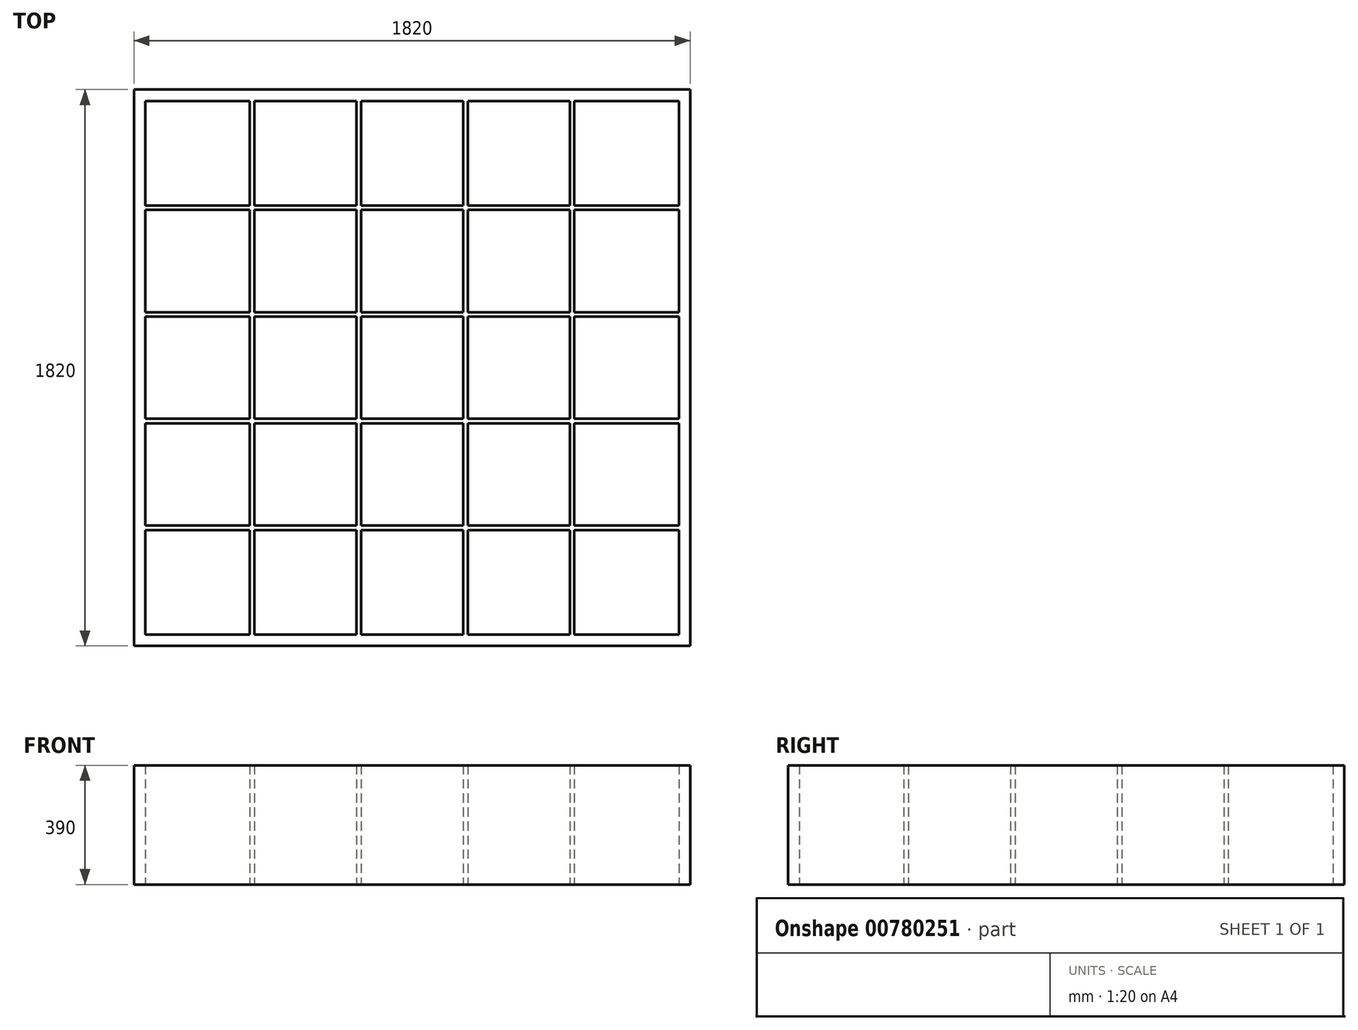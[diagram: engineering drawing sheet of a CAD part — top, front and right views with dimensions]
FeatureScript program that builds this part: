
annotation { "Feature Type Name" : "Feature", "Feature Type Description" : "" }
export const myFeature = defineFeature(function(context is Context, id is Id, definition is map)
    precondition{}
    {
        {
            var Q0;
            Q0=qCreatedBy(makeId("Top.planeOp"),FACE);
            var sketch = newSketch(context, id + "F0", { "sketchPlane" : qUnion([Q0])});
            skLineSegment(sketch, "E0.bottom", {"start": v(910, 910) * mm, "end": v(-910, 910) * mm});
            skLineSegment(sketch, "E0.top", {"start": v(910, -910) * mm, "end": v(-910, -910) * mm});
            skLineSegment(sketch, "E0.left", {"start": v(910, 910) * mm, "end": v(910, -910) * mm});
            skLineSegment(sketch, "E0.right", {"start": v(-910, 910) * mm, "end": v(-910, -910) * mm});
            skPoint(sketch, "E0.middle", {"position": v(0, 0) * mm});
            skLineSegment(sketch, "E1.0", {"start": v(-873, 873) * mm, "end": v(-873, 531.3) * mm});
            skLineSegment(sketch, "E1.1", {"start": v(873, 873) * mm, "end": v(531.3, 873) * mm});
            skLineSegment(sketch, "E1.2", {"start": v(873, 873) * mm, "end": v(873, 531.3) * mm});
            skLineSegment(sketch, "E1.3", {"start": v(873, -873) * mm, "end": v(531.3, -873) * mm});
            skLineSegment(sketch, "E2", {"start": v(-523.8, -873) * mm, "end": v(-523.8, 873) * mm, "construction": true});
            skLineSegment(sketch, "E3.0", {"start": v(-516.3, -873) * mm, "end": v(-516.3, 873) * mm});
            skLineSegment(sketch, "E4.0", {"start": v(-531.3, -873) * mm, "end": v(-531.3, 873) * mm});
            skLineSegment(sketch, "E5.1.0.0", {"start": v(-167.1, -873) * mm, "end": v(-167.1, 873) * mm});
            skLineSegment(sketch, "E5.1.0.1", {"start": v(-174.6, -873) * mm, "end": v(-174.6, 873) * mm, "construction": true});
            skLineSegment(sketch, "E5.1.0.2", {"start": v(-182.1, -873) * mm, "end": v(-182.1, 873) * mm});
            skLineSegment(sketch, "E5.2.0.0", {"start": v(182.1, -873) * mm, "end": v(182.1, 873) * mm});
            skLineSegment(sketch, "E5.2.0.1", {"start": v(174.6, -873) * mm, "end": v(174.6, 873) * mm, "construction": true});
            skLineSegment(sketch, "E5.2.0.2", {"start": v(167.1, -873) * mm, "end": v(167.1, 873) * mm});
            skLineSegment(sketch, "E5.3.0.0", {"start": v(531.3, -873) * mm, "end": v(531.3, 873) * mm});
            skLineSegment(sketch, "E5.3.0.1", {"start": v(523.8, -873) * mm, "end": v(523.8, 873) * mm, "construction": true});
            skLineSegment(sketch, "E5.3.0.2", {"start": v(516.3, -873) * mm, "end": v(516.3, 873) * mm});
            skLineSegment(sketch, "E5.direction1", {"start": v(-516.3, -873) * mm, "end": v(-182.1, -873) * mm, "construction": true});
            skLineSegment(sketch, "E6", {"start": v(-873, -523.8) * mm, "end": v(873, -523.8) * mm, "construction": true});
            skLineSegment(sketch, "E7.0", {"start": v(-873, -531.3) * mm, "end": v(873, -531.3) * mm});
            skLineSegment(sketch, "E8.0", {"start": v(-873, -516.3) * mm, "end": v(873, -516.3) * mm});
            skLineSegment(sketch, "E9.0.1.0", {"start": v(-873, -167.1) * mm, "end": v(873, -167.1) * mm});
            skLineSegment(sketch, "E9.0.1.1", {"start": v(-873, -182.1) * mm, "end": v(873, -182.1) * mm});
            skLineSegment(sketch, "E9.0.1.2", {"start": v(-873, -174.6) * mm, "end": v(873, -174.6) * mm, "construction": true});
            skLineSegment(sketch, "E9.0.2.0", {"start": v(-873, 182.1) * mm, "end": v(873, 182.1) * mm});
            skLineSegment(sketch, "E9.0.2.1", {"start": v(-873, 167.1) * mm, "end": v(873, 167.1) * mm});
            skLineSegment(sketch, "E9.0.2.2", {"start": v(-873, 174.6) * mm, "end": v(873, 174.6) * mm, "construction": true});
            skLineSegment(sketch, "E9.0.3.0", {"start": v(-873, 531.3) * mm, "end": v(873, 531.3) * mm});
            skLineSegment(sketch, "E9.0.3.1", {"start": v(-873, 516.3) * mm, "end": v(873, 516.3) * mm});
            skLineSegment(sketch, "E9.0.3.2", {"start": v(-873, 523.8) * mm, "end": v(873, 523.8) * mm, "construction": true});
            skLineSegment(sketch, "E9.direction1", {"start": v(-873, -531.3) * mm, "end": v(-848, -531.3) * mm, "construction": true});
            skLineSegment(sketch, "E10.trimOffspring", {"start": v(873, 516.3) * mm, "end": v(873, 182.1) * mm});
            skLineSegment(sketch, "E11.trimOffspring", {"start": v(873, 167.1) * mm, "end": v(873, -167.1) * mm});
            skLineSegment(sketch, "E12.trimOffspring", {"start": v(-531.3, -873) * mm, "end": v(-873, -873) * mm});
            skLineSegment(sketch, "E13.trimOffspring", {"start": v(-182.1, -873) * mm, "end": v(-516.3, -873) * mm});
            skLineSegment(sketch, "E14.trimOffspring", {"start": v(167.1, -873) * mm, "end": v(-167.1, -873) * mm});
            skLineSegment(sketch, "E15.trimOffspring", {"start": v(-873, -516.3) * mm, "end": v(-873, -182.1) * mm, "construction": true});
            skLineSegment(sketch, "E16.trimOffspring", {"start": v(-873, -531.3) * mm, "end": v(-873, -873) * mm});
            skLineSegment(sketch, "E17.trimOffspring", {"start": v(-873, -182.1) * mm, "end": v(-873, -516.3) * mm});
            skLineSegment(sketch, "E18.trimOffspring", {"start": v(-873, 167.1) * mm, "end": v(-873, -167.1) * mm});
            skLineSegment(sketch, "E19.trimOffspring", {"start": v(-873, 516.3) * mm, "end": v(-873, 182.1) * mm});
            skLineSegment(sketch, "E20.trimOffspring", {"start": v(-531.3, 873) * mm, "end": v(-873, 873) * mm});
            skLineSegment(sketch, "E21.trimOffspring", {"start": v(-182.1, 873) * mm, "end": v(-516.3, 873) * mm});
            skLineSegment(sketch, "E22.trimOffspring", {"start": v(167.1, 873) * mm, "end": v(-167.1, 873) * mm});
            skLineSegment(sketch, "E23.trimOffspring", {"start": v(516.3, 873) * mm, "end": v(182.1, 873) * mm});
            skLineSegment(sketch, "E24.trimOffspring", {"start": v(873, -182.1) * mm, "end": v(873, -516.3) * mm});
            skLineSegment(sketch, "E25.trimOffspring", {"start": v(873, -531.3) * mm, "end": v(873, -873) * mm});
            skLineSegment(sketch, "E26.trimOffspring", {"start": v(516.3, -873) * mm, "end": v(182.1, -873) * mm});
            skSolve(sketch);
        }
        {
            var Q0;
            Q0 = qSketchRegion(id + "F0", true);
            var Q1;
            {var subQ0=sQuery(id+"F0.wireOp",EDGE,"E7.0");var subQ1=sQuery(id+"F0.wireOp",EDGE,"E3.0");var subQ2=makeQuery(id+"F0.imprint","INTERSECT",VERTEX,{"derivedFrom":[subQ1,subQ0]});Q1=makeQuery(id+"F0.imprint","IMPRINT",FACE,{"disambiguationData":[TD([[makeQuery(id+"F0.imprint","IMPRINT",EDGE,{"disambiguationData":[TD([[subQ2,-1.0]])],"derivedFrom":subQ1}),-1.0]])]});}
            var Q2;
            {var subQ0=sQuery(id+"F0.wireOp",EDGE,"E7.0");var subQ1=sQuery(id+"F0.wireOp",EDGE,"E5.1.0.0");var subQ2=makeQuery(id+"F0.imprint","INTERSECT",VERTEX,{"derivedFrom":[subQ1,subQ0]});Q2=makeQuery(id+"F0.imprint","IMPRINT",FACE,{"disambiguationData":[TD([[makeQuery(id+"F0.imprint","IMPRINT",EDGE,{"disambiguationData":[TD([[subQ2,-1.0]])],"derivedFrom":subQ1}),1.0]])]});}
            var Q3;
            {var subQ0=sQuery(id+"F0.wireOp",EDGE,"E7.0");var subQ1=sQuery(id+"F0.wireOp",EDGE,"E5.1.0.0");var subQ2=makeQuery(id+"F0.imprint","INTERSECT",VERTEX,{"derivedFrom":[subQ1,subQ0]});Q3=makeQuery(id+"F0.imprint","IMPRINT",FACE,{"disambiguationData":[TD([[makeQuery(id+"F0.imprint","IMPRINT",EDGE,{"disambiguationData":[TD([[subQ2,-1.0]])],"derivedFrom":subQ1}),-1.0]])]});}
            var Q4;
            {var subQ0=sQuery(id+"F0.wireOp",EDGE,"E8.0");var subQ1=sQuery(id+"F0.wireOp",EDGE,"E5.1.0.0");var subQ2=makeQuery(id+"F0.imprint","INTERSECT",VERTEX,{"derivedFrom":[subQ1,subQ0]});Q4=makeQuery(id+"F0.imprint","IMPRINT",FACE,{"disambiguationData":[TD([[makeQuery(id+"F0.imprint","IMPRINT",EDGE,{"disambiguationData":[TD([[subQ2,-1.0]])],"derivedFrom":subQ1}),1.0]])]});}
            var Q5;
            {var subQ0=sQuery(id+"F0.wireOp",EDGE,"E7.0");var subQ1=sQuery(id+"F0.wireOp",EDGE,"E5.2.0.0");var subQ2=makeQuery(id+"F0.imprint","INTERSECT",VERTEX,{"derivedFrom":[subQ1,subQ0]});Q5=makeQuery(id+"F0.imprint","IMPRINT",FACE,{"disambiguationData":[TD([[makeQuery(id+"F0.imprint","IMPRINT",EDGE,{"disambiguationData":[TD([[subQ2,-1.0]])],"derivedFrom":subQ1}),-1.0]])]});}
            var Q6;
            {var subQ0=sQuery(id+"F0.wireOp",EDGE,"E7.0");var subQ1=sQuery(id+"F0.wireOp",EDGE,"E5.2.0.0");var subQ2=makeQuery(id+"F0.imprint","INTERSECT",VERTEX,{"derivedFrom":[subQ1,subQ0]});Q6=makeQuery(id+"F0.imprint","IMPRINT",FACE,{"disambiguationData":[TD([[makeQuery(id+"F0.imprint","IMPRINT",EDGE,{"disambiguationData":[TD([[subQ2,-1.0]])],"derivedFrom":subQ1}),1.0]])]});}
            var Q7;
            {var subQ0=sQuery(id+"F0.wireOp",EDGE,"E8.0");var subQ1=sQuery(id+"F0.wireOp",EDGE,"E5.2.0.0");var subQ2=makeQuery(id+"F0.imprint","INTERSECT",VERTEX,{"derivedFrom":[subQ1,subQ0]});Q7=makeQuery(id+"F0.imprint","IMPRINT",FACE,{"disambiguationData":[TD([[makeQuery(id+"F0.imprint","IMPRINT",EDGE,{"disambiguationData":[TD([[subQ2,-1.0]])],"derivedFrom":subQ1}),1.0]])]});}
            var Q8;
            {var subQ0=sQuery(id+"F0.wireOp",EDGE,"E7.0");var subQ1=sQuery(id+"F0.wireOp",EDGE,"E5.3.0.0");var subQ2=makeQuery(id+"F0.imprint","INTERSECT",VERTEX,{"derivedFrom":[subQ1,subQ0]});Q8=makeQuery(id+"F0.imprint","IMPRINT",FACE,{"disambiguationData":[TD([[makeQuery(id+"F0.imprint","IMPRINT",EDGE,{"disambiguationData":[TD([[subQ2,-1.0]])],"derivedFrom":subQ1}),1.0]])]});}
            var Q9;
            {var subQ0=sQuery(id+"F0.wireOp",EDGE,"E8.0");var subQ1=sQuery(id+"F0.wireOp",EDGE,"E5.3.0.0");var subQ2=makeQuery(id+"F0.imprint","INTERSECT",VERTEX,{"derivedFrom":[subQ1,subQ0]});Q9=makeQuery(id+"F0.imprint","IMPRINT",FACE,{"disambiguationData":[TD([[makeQuery(id+"F0.imprint","IMPRINT",EDGE,{"disambiguationData":[TD([[subQ2,-1.0]])],"derivedFrom":subQ1}),1.0]])]});}
            var Q10;
            {var subQ0=sQuery(id+"F0.wireOp",EDGE,"E9.0.1.0");var subQ1=sQuery(id+"F0.wireOp",EDGE,"E5.3.0.0");var subQ2=makeQuery(id+"F0.imprint","INTERSECT",VERTEX,{"derivedFrom":[subQ1,subQ0]});Q10=makeQuery(id+"F0.imprint","IMPRINT",FACE,{"disambiguationData":[TD([[makeQuery(id+"F0.imprint","IMPRINT",EDGE,{"disambiguationData":[TD([[subQ2,-1.0]])],"derivedFrom":subQ1}),1.0]])]});}
            var Q11;
            {var subQ0=sQuery(id+"F0.wireOp",EDGE,"E9.0.1.1");var subQ1=sQuery(id+"F0.wireOp",EDGE,"E5.2.0.0");var subQ2=makeQuery(id+"F0.imprint","INTERSECT",VERTEX,{"derivedFrom":[subQ1,subQ0]});Q11=makeQuery(id+"F0.imprint","IMPRINT",FACE,{"disambiguationData":[TD([[makeQuery(id+"F0.imprint","IMPRINT",EDGE,{"disambiguationData":[TD([[subQ2,-1.0]])],"derivedFrom":subQ1}),-1.0]])]});}
            var Q12;
            {var subQ0=sQuery(id+"F0.wireOp",EDGE,"E9.0.1.1");var subQ1=sQuery(id+"F0.wireOp",EDGE,"E5.3.0.0");var subQ2=makeQuery(id+"F0.imprint","INTERSECT",VERTEX,{"derivedFrom":[subQ1,subQ0]});Q12=makeQuery(id+"F0.imprint","IMPRINT",FACE,{"disambiguationData":[TD([[makeQuery(id+"F0.imprint","IMPRINT",EDGE,{"disambiguationData":[TD([[subQ2,-1.0]])],"derivedFrom":subQ1}),1.0]])]});}
            var Q13;
            {var subQ0=sQuery(id+"F0.wireOp",EDGE,"E9.0.2.0");var subQ1=sQuery(id+"F0.wireOp",EDGE,"E5.3.0.0");var subQ2=makeQuery(id+"F0.imprint","INTERSECT",VERTEX,{"derivedFrom":[subQ1,subQ0]});Q13=makeQuery(id+"F0.imprint","IMPRINT",FACE,{"disambiguationData":[TD([[makeQuery(id+"F0.imprint","IMPRINT",EDGE,{"disambiguationData":[TD([[subQ2,-1.0]])],"derivedFrom":subQ1}),1.0]])]});}
            var Q14;
            {var subQ0=sQuery(id+"F0.wireOp",EDGE,"E9.0.2.1");var subQ1=sQuery(id+"F0.wireOp",EDGE,"E5.3.0.0");var subQ2=makeQuery(id+"F0.imprint","INTERSECT",VERTEX,{"derivedFrom":[subQ1,subQ0]});Q14=makeQuery(id+"F0.imprint","IMPRINT",FACE,{"disambiguationData":[TD([[makeQuery(id+"F0.imprint","IMPRINT",EDGE,{"disambiguationData":[TD([[subQ2,-1.0]])],"derivedFrom":subQ1}),1.0]])]});}
            var Q15;
            {var subQ0=sQuery(id+"F0.wireOp",EDGE,"E9.0.2.1");var subQ1=sQuery(id+"F0.wireOp",EDGE,"E5.2.0.0");var subQ2=makeQuery(id+"F0.imprint","INTERSECT",VERTEX,{"derivedFrom":[subQ1,subQ0]});Q15=makeQuery(id+"F0.imprint","IMPRINT",FACE,{"disambiguationData":[TD([[makeQuery(id+"F0.imprint","IMPRINT",EDGE,{"disambiguationData":[TD([[subQ2,-1.0]])],"derivedFrom":subQ1}),-1.0]])]});}
            var Q16;
            {var subQ0=sQuery(id+"F0.wireOp",EDGE,"E9.0.3.1");var subQ1=sQuery(id+"F0.wireOp",EDGE,"E5.2.0.0");var subQ2=makeQuery(id+"F0.imprint","INTERSECT",VERTEX,{"derivedFrom":[subQ1,subQ0]});Q16=makeQuery(id+"F0.imprint","IMPRINT",FACE,{"disambiguationData":[TD([[makeQuery(id+"F0.imprint","IMPRINT",EDGE,{"disambiguationData":[TD([[subQ2,-1.0]])],"derivedFrom":subQ1}),-1.0]])]});}
            var Q17;
            {var subQ0=sQuery(id+"F0.wireOp",EDGE,"E9.0.3.0");var subQ1=sQuery(id+"F0.wireOp",EDGE,"E5.3.0.0");var subQ2=makeQuery(id+"F0.imprint","INTERSECT",VERTEX,{"derivedFrom":[subQ1,subQ0]});Q17=makeQuery(id+"F0.imprint","IMPRINT",FACE,{"disambiguationData":[TD([[makeQuery(id+"F0.imprint","IMPRINT",EDGE,{"disambiguationData":[TD([[subQ2,1.0]])],"derivedFrom":subQ1}),1.0]])]});}
            var Q18;
            {var subQ0=sQuery(id+"F0.wireOp",EDGE,"E9.0.3.1");var subQ1=sQuery(id+"F0.wireOp",EDGE,"E3.0");var subQ2=makeQuery(id+"F0.imprint","INTERSECT",VERTEX,{"derivedFrom":[subQ1,subQ0]});Q18=makeQuery(id+"F0.imprint","IMPRINT",FACE,{"disambiguationData":[TD([[makeQuery(id+"F0.imprint","IMPRINT",EDGE,{"disambiguationData":[TD([[subQ2,-1.0]])],"derivedFrom":subQ1}),-1.0]])]});}
            var Q19;
            {var subQ0=sQuery(id+"F0.wireOp",EDGE,"E9.0.3.1");var subQ1=sQuery(id+"F0.wireOp",EDGE,"E3.0");var subQ2=makeQuery(id+"F0.imprint","INTERSECT",VERTEX,{"derivedFrom":[subQ1,subQ0]});Q19=makeQuery(id+"F0.imprint","IMPRINT",FACE,{"disambiguationData":[TD([[makeQuery(id+"F0.imprint","IMPRINT",EDGE,{"disambiguationData":[TD([[subQ2,-1.0]])],"derivedFrom":subQ1}),1.0]])]});}
            var Q20;
            {var subQ0=sQuery(id+"F0.wireOp",EDGE,"E9.0.2.0");var subQ1=sQuery(id+"F0.wireOp",EDGE,"E3.0");var subQ2=makeQuery(id+"F0.imprint","INTERSECT",VERTEX,{"derivedFrom":[subQ1,subQ0]});Q20=makeQuery(id+"F0.imprint","IMPRINT",FACE,{"disambiguationData":[TD([[makeQuery(id+"F0.imprint","IMPRINT",EDGE,{"disambiguationData":[TD([[subQ2,-1.0]])],"derivedFrom":subQ1}),1.0]])]});}
            var Q21;
            {var subQ0=sQuery(id+"F0.wireOp",EDGE,"E9.0.2.0");var subQ1=sQuery(id+"F0.wireOp",EDGE,"E5.1.0.0");var subQ2=makeQuery(id+"F0.imprint","INTERSECT",VERTEX,{"derivedFrom":[subQ1,subQ0]});Q21=makeQuery(id+"F0.imprint","IMPRINT",FACE,{"disambiguationData":[TD([[makeQuery(id+"F0.imprint","IMPRINT",EDGE,{"disambiguationData":[TD([[subQ2,-1.0]])],"derivedFrom":subQ1}),1.0]])]});}
            var Q22;
            {var subQ0=sQuery(id+"F0.wireOp",EDGE,"E9.0.3.1");var subQ1=sQuery(id+"F0.wireOp",EDGE,"E5.1.0.0");var subQ2=makeQuery(id+"F0.imprint","INTERSECT",VERTEX,{"derivedFrom":[subQ1,subQ0]});Q22=makeQuery(id+"F0.imprint","IMPRINT",FACE,{"disambiguationData":[TD([[makeQuery(id+"F0.imprint","IMPRINT",EDGE,{"disambiguationData":[TD([[subQ2,-1.0]])],"derivedFrom":subQ1}),1.0]])]});}
            var Q23;
            {var subQ0=sQuery(id+"F0.wireOp",EDGE,"E9.0.3.1");var subQ1=sQuery(id+"F0.wireOp",EDGE,"E5.1.0.0");var subQ2=makeQuery(id+"F0.imprint","INTERSECT",VERTEX,{"derivedFrom":[subQ1,subQ0]});Q23=makeQuery(id+"F0.imprint","IMPRINT",FACE,{"disambiguationData":[TD([[makeQuery(id+"F0.imprint","IMPRINT",EDGE,{"disambiguationData":[TD([[subQ2,-1.0]])],"derivedFrom":subQ1}),-1.0]])]});}
            var Q24;
            {var subQ0=sQuery(id+"F0.wireOp",EDGE,"E9.0.2.1");var subQ1=sQuery(id+"F0.wireOp",EDGE,"E3.0");var subQ2=makeQuery(id+"F0.imprint","INTERSECT",VERTEX,{"derivedFrom":[subQ1,subQ0]});Q24=makeQuery(id+"F0.imprint","IMPRINT",FACE,{"disambiguationData":[TD([[makeQuery(id+"F0.imprint","IMPRINT",EDGE,{"disambiguationData":[TD([[subQ2,-1.0]])],"derivedFrom":subQ1}),1.0]])]});}
            var Q25;
            {var subQ0=sQuery(id+"F0.wireOp",EDGE,"E9.0.2.1");var subQ1=sQuery(id+"F0.wireOp",EDGE,"E3.0");var subQ2=makeQuery(id+"F0.imprint","INTERSECT",VERTEX,{"derivedFrom":[subQ1,subQ0]});Q25=makeQuery(id+"F0.imprint","IMPRINT",FACE,{"disambiguationData":[TD([[makeQuery(id+"F0.imprint","IMPRINT",EDGE,{"disambiguationData":[TD([[subQ2,-1.0]])],"derivedFrom":subQ1}),-1.0]])]});}
            var Q26;
            {var subQ0=sQuery(id+"F0.wireOp",EDGE,"E9.0.1.0");var subQ1=sQuery(id+"F0.wireOp",EDGE,"E3.0");var subQ2=makeQuery(id+"F0.imprint","INTERSECT",VERTEX,{"derivedFrom":[subQ1,subQ0]});Q26=makeQuery(id+"F0.imprint","IMPRINT",FACE,{"disambiguationData":[TD([[makeQuery(id+"F0.imprint","IMPRINT",EDGE,{"disambiguationData":[TD([[subQ2,-1.0]])],"derivedFrom":subQ1}),1.0]])]});}
            var Q27;
            {var subQ0=sQuery(id+"F0.wireOp",EDGE,"E9.0.1.0");var subQ1=sQuery(id+"F0.wireOp",EDGE,"E5.1.0.0");var subQ2=makeQuery(id+"F0.imprint","INTERSECT",VERTEX,{"derivedFrom":[subQ1,subQ0]});Q27=makeQuery(id+"F0.imprint","IMPRINT",FACE,{"disambiguationData":[TD([[makeQuery(id+"F0.imprint","IMPRINT",EDGE,{"disambiguationData":[TD([[subQ2,-1.0]])],"derivedFrom":subQ1}),1.0]])]});}
            var Q28;
            {var subQ0=sQuery(id+"F0.wireOp",EDGE,"E9.0.2.1");var subQ1=sQuery(id+"F0.wireOp",EDGE,"E5.1.0.0");var subQ2=makeQuery(id+"F0.imprint","INTERSECT",VERTEX,{"derivedFrom":[subQ1,subQ0]});Q28=makeQuery(id+"F0.imprint","IMPRINT",FACE,{"disambiguationData":[TD([[makeQuery(id+"F0.imprint","IMPRINT",EDGE,{"disambiguationData":[TD([[subQ2,-1.0]])],"derivedFrom":subQ1}),-1.0]])]});}
            var Q29;
            {var subQ0=sQuery(id+"F0.wireOp",EDGE,"E9.0.2.1");var subQ1=sQuery(id+"F0.wireOp",EDGE,"E5.1.0.0");var subQ2=makeQuery(id+"F0.imprint","INTERSECT",VERTEX,{"derivedFrom":[subQ1,subQ0]});Q29=makeQuery(id+"F0.imprint","IMPRINT",FACE,{"disambiguationData":[TD([[makeQuery(id+"F0.imprint","IMPRINT",EDGE,{"disambiguationData":[TD([[subQ2,-1.0]])],"derivedFrom":subQ1}),1.0]])]});}
            var Q30;
            {var subQ0=sQuery(id+"F0.wireOp",EDGE,"E9.0.1.1");var subQ1=sQuery(id+"F0.wireOp",EDGE,"E3.0");var subQ2=makeQuery(id+"F0.imprint","INTERSECT",VERTEX,{"derivedFrom":[subQ1,subQ0]});Q30=makeQuery(id+"F0.imprint","IMPRINT",FACE,{"disambiguationData":[TD([[makeQuery(id+"F0.imprint","IMPRINT",EDGE,{"disambiguationData":[TD([[subQ2,-1.0]])],"derivedFrom":subQ1}),-1.0]])]});}
            var Q31;
            {var subQ0=sQuery(id+"F0.wireOp",EDGE,"E8.0");var subQ1=sQuery(id+"F0.wireOp",EDGE,"E3.0");var subQ2=makeQuery(id+"F0.imprint","INTERSECT",VERTEX,{"derivedFrom":[subQ1,subQ0]});Q31=makeQuery(id+"F0.imprint","IMPRINT",FACE,{"disambiguationData":[TD([[makeQuery(id+"F0.imprint","IMPRINT",EDGE,{"disambiguationData":[TD([[subQ2,-1.0]])],"derivedFrom":subQ1}),1.0]])]});}
            var Q32;
            {var subQ0=sQuery(id+"F0.wireOp",EDGE,"E9.0.1.1");var subQ1=sQuery(id+"F0.wireOp",EDGE,"E3.0");var subQ2=makeQuery(id+"F0.imprint","INTERSECT",VERTEX,{"derivedFrom":[subQ1,subQ0]});Q32=makeQuery(id+"F0.imprint","IMPRINT",FACE,{"disambiguationData":[TD([[makeQuery(id+"F0.imprint","IMPRINT",EDGE,{"disambiguationData":[TD([[subQ2,-1.0]])],"derivedFrom":subQ1}),1.0]])]});}
            var Q33;
            {var subQ0=sQuery(id+"F0.wireOp",EDGE,"E9.0.1.1");var subQ1=sQuery(id+"F0.wireOp",EDGE,"E5.1.0.0");var subQ2=makeQuery(id+"F0.imprint","INTERSECT",VERTEX,{"derivedFrom":[subQ1,subQ0]});Q33=makeQuery(id+"F0.imprint","IMPRINT",FACE,{"disambiguationData":[TD([[makeQuery(id+"F0.imprint","IMPRINT",EDGE,{"disambiguationData":[TD([[subQ2,-1.0]])],"derivedFrom":subQ1}),-1.0]])]});}
            var Q34;
            {var subQ0=sQuery(id+"F0.wireOp",EDGE,"E9.0.1.1");var subQ1=sQuery(id+"F0.wireOp",EDGE,"E5.1.0.0");var subQ2=makeQuery(id+"F0.imprint","INTERSECT",VERTEX,{"derivedFrom":[subQ1,subQ0]});Q34=makeQuery(id+"F0.imprint","IMPRINT",FACE,{"disambiguationData":[TD([[makeQuery(id+"F0.imprint","IMPRINT",EDGE,{"disambiguationData":[TD([[subQ2,-1.0]])],"derivedFrom":subQ1}),1.0]])]});}
            var Q35;
            {var subQ0=sQuery(id+"F0.wireOp",EDGE,"E7.0");var subQ1=sQuery(id+"F0.wireOp",EDGE,"E3.0");var subQ2=makeQuery(id+"F0.imprint","INTERSECT",VERTEX,{"derivedFrom":[subQ1,subQ0]});Q35=makeQuery(id+"F0.imprint","IMPRINT",FACE,{"disambiguationData":[TD([[makeQuery(id+"F0.imprint","IMPRINT",EDGE,{"disambiguationData":[TD([[subQ2,-1.0]])],"derivedFrom":subQ1}),1.0]])]});}
            var Q36;
            {var subQ0=sQuery(id+"F0.wireOp",EDGE,"E9.0.1.0");var subQ1=sQuery(id+"F0.wireOp",EDGE,"E5.2.0.0");var subQ2=makeQuery(id+"F0.imprint","INTERSECT",VERTEX,{"derivedFrom":[subQ1,subQ0]});Q36=makeQuery(id+"F0.imprint","IMPRINT",FACE,{"disambiguationData":[TD([[makeQuery(id+"F0.imprint","IMPRINT",EDGE,{"disambiguationData":[TD([[subQ2,-1.0]])],"derivedFrom":subQ1}),1.0]])]});}
            var Q37;
            {var subQ0=sQuery(id+"F0.wireOp",EDGE,"E9.0.1.1");var subQ1=sQuery(id+"F0.wireOp",EDGE,"E5.2.0.0");var subQ2=makeQuery(id+"F0.imprint","INTERSECT",VERTEX,{"derivedFrom":[subQ1,subQ0]});Q37=makeQuery(id+"F0.imprint","IMPRINT",FACE,{"disambiguationData":[TD([[makeQuery(id+"F0.imprint","IMPRINT",EDGE,{"disambiguationData":[TD([[subQ2,-1.0]])],"derivedFrom":subQ1}),1.0]])]});}
            var Q38;
            {var subQ0=sQuery(id+"F0.wireOp",EDGE,"E9.0.2.0");var subQ1=sQuery(id+"F0.wireOp",EDGE,"E5.2.0.0");var subQ2=makeQuery(id+"F0.imprint","INTERSECT",VERTEX,{"derivedFrom":[subQ1,subQ0]});Q38=makeQuery(id+"F0.imprint","IMPRINT",FACE,{"disambiguationData":[TD([[makeQuery(id+"F0.imprint","IMPRINT",EDGE,{"disambiguationData":[TD([[subQ2,-1.0]])],"derivedFrom":subQ1}),1.0]])]});}
            var Q39;
            {var subQ0=sQuery(id+"F0.wireOp",EDGE,"E9.0.2.1");var subQ1=sQuery(id+"F0.wireOp",EDGE,"E5.2.0.0");var subQ2=makeQuery(id+"F0.imprint","INTERSECT",VERTEX,{"derivedFrom":[subQ1,subQ0]});Q39=makeQuery(id+"F0.imprint","IMPRINT",FACE,{"disambiguationData":[TD([[makeQuery(id+"F0.imprint","IMPRINT",EDGE,{"disambiguationData":[TD([[subQ2,-1.0]])],"derivedFrom":subQ1}),1.0]])]});}
            var Q40;
            {var subQ0=sQuery(id+"F0.wireOp",EDGE,"E9.0.3.1");var subQ1=sQuery(id+"F0.wireOp",EDGE,"E5.2.0.0");var subQ2=makeQuery(id+"F0.imprint","INTERSECT",VERTEX,{"derivedFrom":[subQ1,subQ0]});Q40=makeQuery(id+"F0.imprint","IMPRINT",FACE,{"disambiguationData":[TD([[makeQuery(id+"F0.imprint","IMPRINT",EDGE,{"disambiguationData":[TD([[subQ2,-1.0]])],"derivedFrom":subQ1}),1.0]])]});}
            extrude(context, id + "F1", {"entities" : qUnion([Q0, Q1, Q2, Q3, Q4, Q5, Q6, Q7, Q8, Q9, Q10, Q11, Q12, Q13, Q14, Q15, Q16, Q17, Q18, Q19, Q20, Q21, Q22, Q23, Q24, Q25, Q26, Q27, Q28, Q29, Q30, Q31, Q32, Q33, Q34, Q35, Q36, Q37, Q38, Q39, Q40]), "depth" : 390 * mm, "offsetDistance" : 25 * mm});
        }
    });
